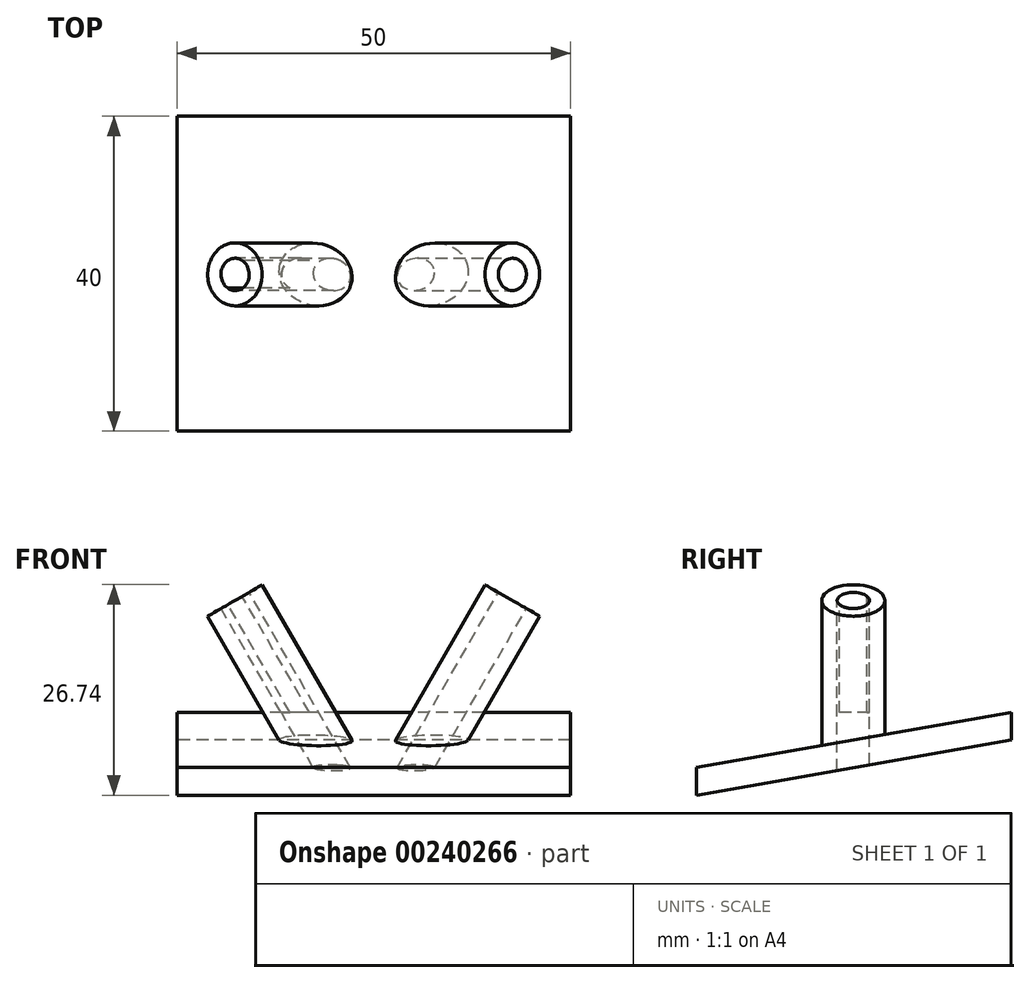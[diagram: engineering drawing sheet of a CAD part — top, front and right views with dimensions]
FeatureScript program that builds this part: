
annotation { "Feature Type Name" : "Feature", "Feature Type Description" : "" }
export const myFeature = defineFeature(function(context is Context, id is Id, definition is map)
    precondition{}
    {
        {
            var Q0;
            Q0=qCreatedBy(makeId("Top.planeOp"),FACE);
            var sketch = newSketch(context, id + "F0", { "sketchPlane" : qUnion([Q0])});
            skLineSegment(sketch, "E0.bottom", {"start": v(25, -20) * mm, "end": v(-25, -20) * mm});
            skLineSegment(sketch, "E0.top", {"start": v(25, 20) * mm, "end": v(-25, 20) * mm});
            skLineSegment(sketch, "E0.left", {"start": v(25, -20) * mm, "end": v(25, 20) * mm});
            skLineSegment(sketch, "E0.right", {"start": v(-25, -20) * mm, "end": v(-25, 20) * mm});
            skPoint(sketch, "E0.middle", {"position": v(0, 0) * mm});
            skSolve(sketch);
        }
        {
            var Q0;
            Q0 = qSketchRegion(id + "F0", true);
            extrude(context, id + "F1", {"entities" : qUnion([Q0]), "depth" : 2.5 * mm});
        }
        {
            var Q0;
            Q0=qCreatedBy(makeId("Front.planeOp"),FACE);
            var sketch = newSketch(context, id + "F2", { "sketchPlane" : qUnion([Q0])});
            skLineSegment(sketch, "E1", {"start": v(22.6, 13.86) * mm, "end": v(20, 15.36) * mm});
            skLineSegment(sketch, "E2.MirrorCS", {"start": v(-22.6, 13.86) * mm, "end": v(-20, 15.36) * mm});
            skSolve(sketch);
        }
        {
            var Q0;
            Q0 = qSketchRegion(id + "F2", true);
            var Q1;
            Q1 = qConstructionFilter(qBodyType(qCreatedBy(id + "F2" ,EDGE), BodyType.WIRE), ConstructionObject.NO);
            extrude(context, id + "F3", {"entities" : qUnion([Q0]), "bodyType" : ToolBodyType.SURFACE, "surfaceEntities" : qUnion([Q1]), "endBound" : BoundingType.SYMMETRIC, "depth" : 25 * mm});
        }
        {
            var Q0;
            Q0=makeQuery(id+"F3.opExtrude","SWEPT_FACE",FACE,{"disambiguationData":[OSD([sQuery(id+"F2.wireOp",EDGE,"E1")])]});
            cPlane(context, id + "F4", {"entities" : qUnion([Q0]), "cplaneType" : CPlaneType.OFFSET, "offset" : 0 * mm, "width" : 150 * mm, "height" : 150 * mm});
        }
        {
            var Q0;
            Q0=makeQuery(id+"F3.opExtrude","SWEPT_FACE",FACE,{"disambiguationData":[OSD([sQuery(id+"F2.wireOp",EDGE,"E2.MirrorCS")])]});
            cPlane(context, id + "F5", {"entities" : qUnion([Q0]), "cplaneType" : CPlaneType.OFFSET, "offset" : 0 * mm, "width" : 150 * mm, "height" : 150 * mm});
        }
        {
            var Q0;
            Q0=qCreatedBy(id+"F5.planeOp",FACE);
            var sketch = newSketch(context, id + "F6", { "sketchPlane" : qUnion([Q0])});
            skCircle(sketch, "E3.0", {"center": v(-6.86, 0.1) * mm, "radius": 2.05 * mm});
            skSolve(sketch);
        }
        {
            var Q0;
            Q0=qCreatedBy(id+"F5.planeOp",FACE);
            var sketch = newSketch(context, id + "F7", { "sketchPlane" : qUnion([Q0])});
            skCircle(sketch, "E4", {"center": v(-6.89, 0.08) * mm, "radius": 4 * mm});
            skCircle(sketch, "E5.0", {"center": v(-6.89, 0.08) * mm, "radius": 2.05 * mm});
            skSolve(sketch);
        }
        {
            var Q0;
            Q0 = qSketchRegion(id + "F7", true);
            var Q1;
            Q1=makeQuery(id+"F1.opExtrude","CAP_FACE",FACE,{"disambiguationData":[OSD([sQuery(id+"F0.wireOp",EDGE,"E0.bottom"),sQuery(id+"F0.wireOp",EDGE,"E0.top"),sQuery(id+"F0.wireOp",EDGE,"E0.left"),sQuery(id+"F0.wireOp",EDGE,"E0.right")])],"isStart":true});
            extrude(context, id + "F8", {"entities" : qUnion([Q0]), "operationType" : NewBodyOperationType.ADD, "endBound" : BoundingType.UP_TO_SURFACE, "endBoundEntityFace" : qUnion([Q1]), "depth" : 19.4 * mm});
        }
        {
            var Q0;
            Q0=makeQuery(id+"F1.opExtrude","SWEPT_BODY",BODY,{"disambiguationData":[OSD([sQuery(id+"F0.wireOp",EDGE,"E0.bottom"),sQuery(id+"F0.wireOp",EDGE,"E0.top"),sQuery(id+"F0.wireOp",EDGE,"E0.left"),sQuery(id+"F0.wireOp",EDGE,"E0.right")])]});
            var Q1;
            Q1=qCreatedBy(makeId("Right.planeOp"),FACE);
            mirror(context, id + "F9", {"operationType" : NewBodyOperationType.ADD, "entities" : qUnion([Q0]), "mirrorPlane" : qUnion([Q1])});
        }
        {
            var Q0;
            Q0 = qSketchRegion(id + "F0", true);
            extrude(context, id + "F10", {"entities" : qUnion([Q0]), "operationType" : NewBodyOperationType.ADD, "oppositeDirection" : true, "depth" : 8 * mm});
        }
        {
            var Q0;
            Q0=makeQuery(id+"F10.opExtrude","CAP_EDGE",EDGE,{"disambiguationData":[OSD([sQuery(id+"F0.wireOp",EDGE,"E0.top")])],"isStart":false});
            chamfer(context, id + "F11", {"entities" : qUnion([Q0]), "chamferType" : ChamferType.TWO_OFFSETS, "width1" : 7 * mm, "oppositeDirection" : false, "width2" : 40 * mm, "tangentPropagation" : true});
        }
        {
            var Q0;
            Q0 = qSketchRegion(id + "F6", true);
            extrude(context, id + "F12", {"entities" : qUnion([Q0]), "operationType" : NewBodyOperationType.REMOVE, "depth" : 46.3 * mm});
        }
        {
            var Q0;
            Q0=qCreatedBy(id+"F4.planeOp",FACE);
            var sketch = newSketch(context, id + "F13", { "sketchPlane" : qUnion([Q0])});
            skCircle(sketch, "E6.0", {"center": v(6.89, -0.08) * mm, "radius": 2.05 * mm});
            skSolve(sketch);
        }
        {
            var Q0;
            Q0 = qSketchRegion(id + "F13", true);
            extrude(context, id + "F14", {"entities" : qUnion([Q0]), "operationType" : NewBodyOperationType.REMOVE, "oppositeDirection" : true, "depth" : 68.7 * mm});
        }
        {
            var Q0;
            Q0=makeQuery(id+"F1.opExtrude","CAP_EDGE",EDGE,{"disambiguationData":[OSD([sQuery(id+"F0.wireOp",EDGE,"E0.bottom")])],"isStart":false});
            chamfer(context, id + "F15", {"entities" : qUnion([Q0]), "chamferType" : ChamferType.TWO_OFFSETS, "width1" : 7 * mm, "oppositeDirection" : false, "width2" : 40 * mm, "tangentPropagation" : true});
        }
    });
